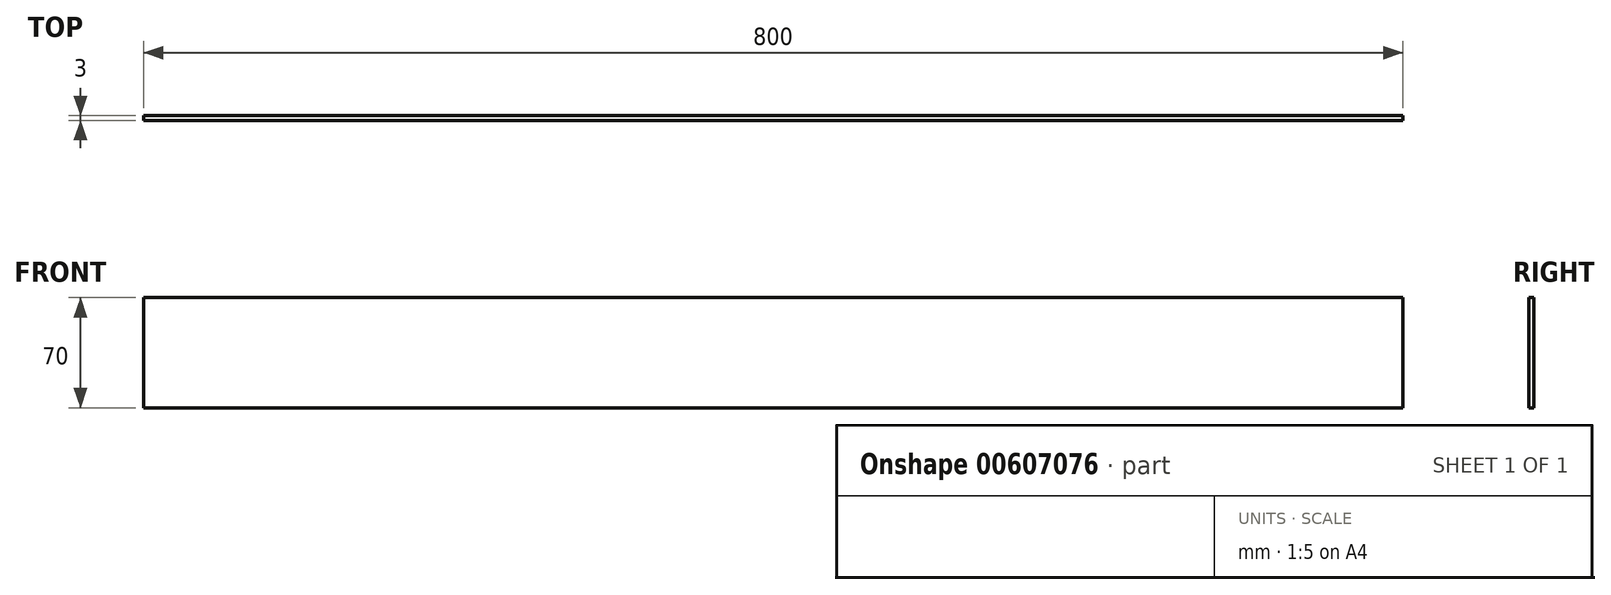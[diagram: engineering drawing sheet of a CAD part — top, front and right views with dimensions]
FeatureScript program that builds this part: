
annotation { "Feature Type Name" : "Feature", "Feature Type Description" : "" }
export const myFeature = defineFeature(function(context is Context, id is Id, definition is map)
    precondition{}
    {
        {
            var Q0;
            Q0=qCreatedBy(makeId("Front.planeOp"),FACE);
            var sketch = newSketch(context, id + "F0", { "sketchPlane" : qUnion([Q0]) });
            skLineSegment(sketch, "E0.bottom", {"start": v(400, 35) * mm, "end": v(-400, 35) * mm});
            skLineSegment(sketch, "E0.top", {"start": v(400, -35) * mm, "end": v(-400, -35) * mm});
            skLineSegment(sketch, "E0.left", {"start": v(400, 35) * mm, "end": v(400, -35) * mm});
            skLineSegment(sketch, "E0.right", {"start": v(-400, 35) * mm, "end": v(-400, -35) * mm});
            skPoint(sketch, "E0.middle", {"position": v(0, 0) * mm});
            skSolve(sketch);
        }
        {
            var Q0;
            Q0=makeQuery(id+"F0.imprint","IMPRINT",FACE,{"disambiguationData":[TD([[makeQuery(id+"F0.imprint","IMPRINT",EDGE,{"derivedFrom":sQuery(id+"F0.wireOp",EDGE,"E0.bottom")}),1.0]])]});
            extrude(context, id + "F1", {"entities" : qUnion([Q0]), "depth" : 3 * mm, "offsetDistance" : 25 * mm});
        }
    });
